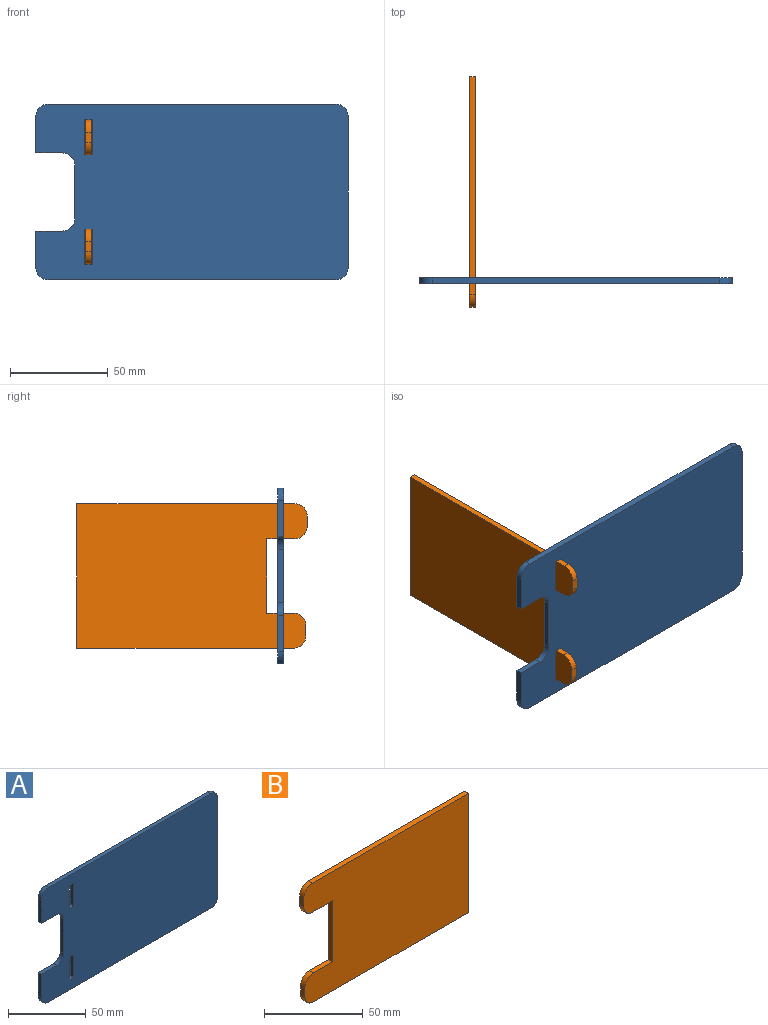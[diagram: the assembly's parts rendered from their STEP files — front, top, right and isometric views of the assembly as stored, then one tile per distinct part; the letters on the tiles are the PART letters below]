
ASSEMBLY  parts=2 mates=1
PART A: 24 faces, bbox 160x3x90 mm
  f0: plane 18x3mm, normal (1,0,0), area 54mm2, adj f1,f21,f22,f23
  f1: plane 4x3mm, normal (0,0,-1), area 12mm2, adj f0,f2,f22,f23
  f2: plane 18x3mm, normal (-1,0,0), area 54mm2, adj f1,f21,f22,f23
  f3: plane 18x3mm, normal (1,0,0), area 54mm2, adj f4,f19,f22,f23
  f4: plane 4x3mm, normal (0,0,-1), area 12mm2, adj f3,f5,f22,f23
  f5: plane 18x3mm, normal (-1,0,0), area 54mm2, adj f4,f19,f22,f23
  f6: plane 18.65x3mm, normal (-1,0,0), area 56mm2, adj f7,f20,f22,f23
  f7: plane 13.65x3mm, normal (0,0,-1), area 40.9mm2, adj f6,f8,f22,f23
  f8: cylinder r=6.35mm len=6.35mm, axis (0,1,0), area 29.9mm2, adj f7,f9,f22,f23
  f9: plane 27.3x3mm, normal (-1,0,0), area 81.9mm2, adj f8,f10,f22,f23
  f10: cylinder r=6.35mm len=6.35mm, axis (0,1,0), area 29.9mm2, adj f9,f11,f22,f23
  f11: plane 13.65x3mm, normal (0,0,1), area 40.9mm2, adj f10,f12,f22,f23
  f12: plane 18.65x3mm, normal (-1,0,0), area 56mm2, adj f11,f13,f22,f23
  f13: cylinder r=6.35mm len=6.35mm, axis (0,1,0), area 29.9mm2, adj f12,f14,f22,f23
  f14: plane 147.3x3mm, normal (0,0,-1), area 441.9mm2, adj f13,f15,f22,f23
  f15: cylinder r=6.35mm len=6.35mm, axis (0,1,0), area 29.9mm2, adj f14,f16,f22,f23
  f16: plane 77.3x3mm, normal (1,0,0), area 231.9mm2, adj f15,f17,f22,f23
  f17: cylinder r=6.35mm len=6.35mm, axis (0,1,0), area 29.9mm2, adj f16,f18,f22,f23
  f18: plane 147.3x3mm, normal (0,0,1), area 441.9mm2, adj f17,f20,f22,f23
  f19: plane 4x3mm, normal (0,0,1), area 12mm2, adj f3,f5,f22,f23
  f20: cylinder r=6.35mm len=6.35mm, axis (0,1,0), area 29.9mm2, adj f6,f18,f22,f23
  f21: plane 4x3mm, normal (0,0,1), area 12mm2, adj f0,f2,f22,f23
  f22: plane 160x90mm, normal (0,-1,0), area 13438.7mm2, adj f0,f1,f2,f3,f4,f5,f6,f7
  f23: plane 160x90mm, normal (0,1,0), area 13438.7mm2, adj f0,f1,f2,f3,f4,f5,f6,f7
PART B: 14 faces, bbox 118x3x74 mm
  f0: plane 111.63x3mm, normal (0,0,1), area 334.9mm2, adj f1,f11,f12,f13
  f1: cylinder r=6.35mm len=6.35mm, axis (0,1,0), area 29.9mm2, adj f0,f2,f12,f13
  f2: plane 5.3x3mm, normal (-1,0,0), area 15.9mm2, adj f1,f3,f12,f13
  f3: cylinder r=6.35mm len=6.35mm, axis (0,1,0), area 29.9mm2, adj f2,f4,f12,f13
  f4: plane 14.32x3mm, normal (0,0,-1), area 42.9mm2, adj f3,f5,f12,f13
  f5: plane 38x3mm, normal (-1,0,0), area 114mm2, adj f4,f6,f12,f13
  f6: plane 13.65x3mm, normal (0,0,1), area 41mm2, adj f5,f7,f12,f13
  f7: cylinder r=6.35mm len=6.35mm, axis (0,1,0), area 29.9mm2, adj f6,f8,f12,f13
  f8: plane 5.3x3mm, normal (-1,0,0), area 15.9mm2, adj f7,f9,f12,f13
  f9: cylinder r=6.35mm len=6.35mm, axis (0,1,0), area 29.9mm2, adj f8,f10,f12,f13
  f10: plane 110.96x3mm, normal (0,0,-1), area 332.9mm2, adj f9,f11,f12,f13
  f11: plane 74x3mm, normal (1,0,0), area 222mm2, adj f0,f10,f12,f13
  f12: plane 117.98x74mm, normal (0,-1,0), area 7898.5mm2, adj f0,f1,f2,f3,f4,f5,f6,f7
  f13: plane 117.98x74mm, normal (0,1,0), area 7898.5mm2, adj f0,f1,f2,f3,f4,f5,f6,f7
PLACE A t=(-11.64,-4.48,-12)mm
PLACE B rot(axis=(0,0,1),90deg) t=(-99.34,76.87,167.12)mm
MATE slider B.f4 <-> A.f19  axis (0,0,-1) through (-97.84,-5.98,52)mm
